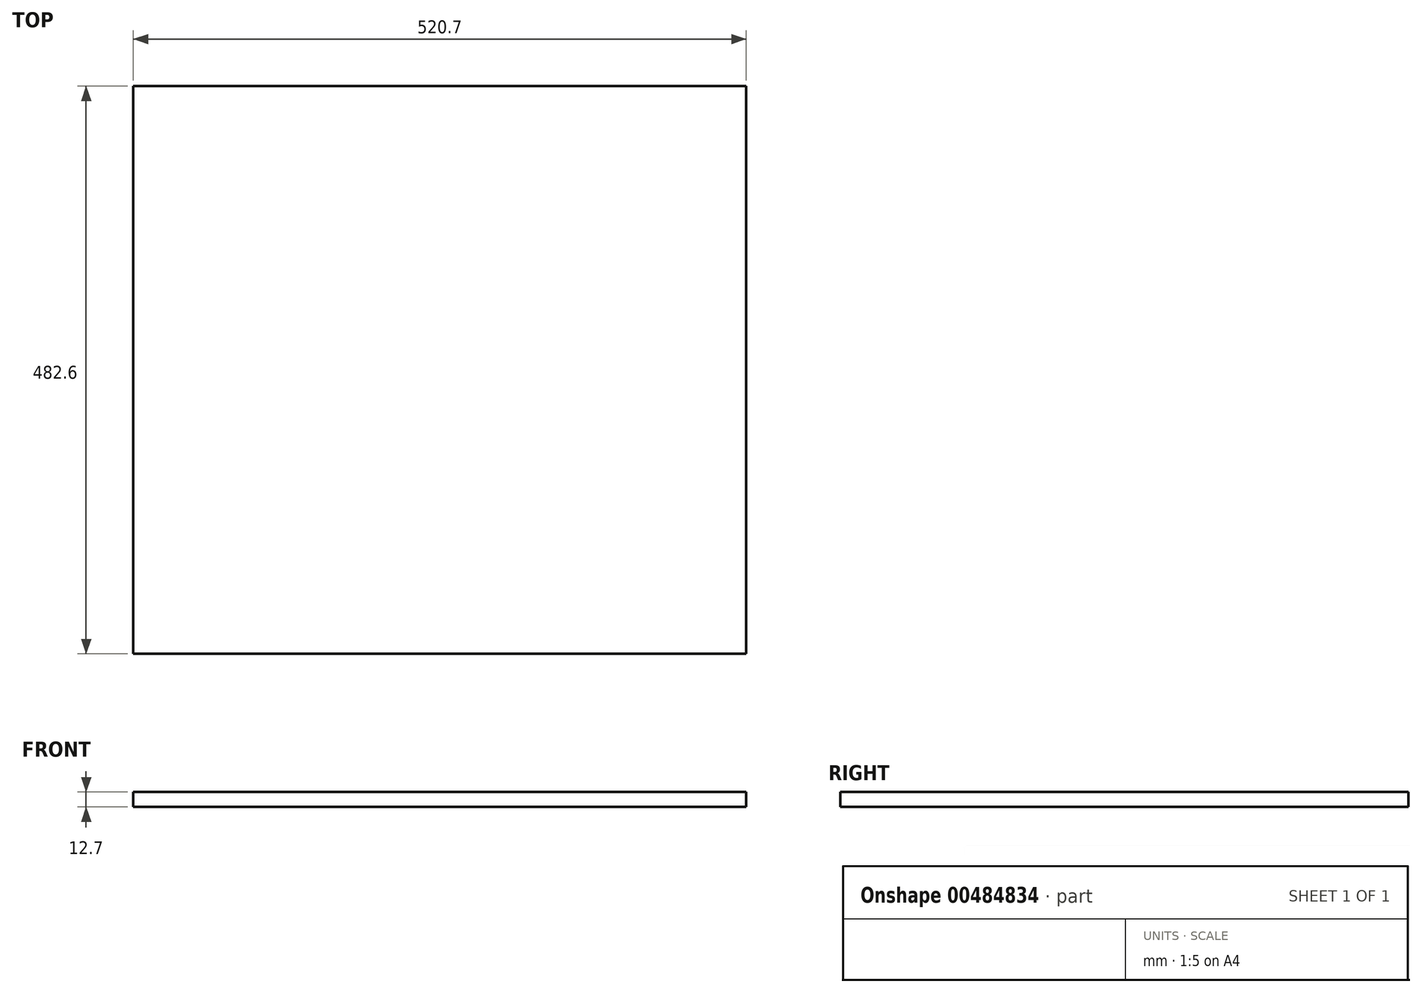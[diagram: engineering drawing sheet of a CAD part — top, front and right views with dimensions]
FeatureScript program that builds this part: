
annotation { "Feature Type Name" : "Feature", "Feature Type Description" : "" }
export const myFeature = defineFeature(function(context is Context, id is Id, definition is map)
    precondition{}
    {
        {
            var Q0;
            Q0=qCreatedBy(makeId("Top.planeOp"),FACE);
            var sketch = newSketch(context, id + "F0", { "sketchPlane" : qUnion([Q0])});
            skLineSegment(sketch, "E0.bottom", {"start": v(260.35, 241.3) * mm, "end": v(-260.35, 241.3) * mm});
            skLineSegment(sketch, "E0.top", {"start": v(260.35, -241.3) * mm, "end": v(-260.35, -241.3) * mm});
            skLineSegment(sketch, "E0.left", {"start": v(260.35, 241.3) * mm, "end": v(260.35, -241.3) * mm});
            skLineSegment(sketch, "E0.right", {"start": v(-260.35, 241.3) * mm, "end": v(-260.35, -241.3) * mm});
            skPoint(sketch, "E0.middle", {"position": v(0, 0) * mm});
            skSolve(sketch);
        }
        {
            var Q0;
            Q0 = qSketchRegion(id + "F0", true);
            extrude(context, id + "F1", {"entities" : qUnion([Q0]), "depth" : 12.7 * mm, "offsetDistance" : 25.4 * mm});
        }
    });
